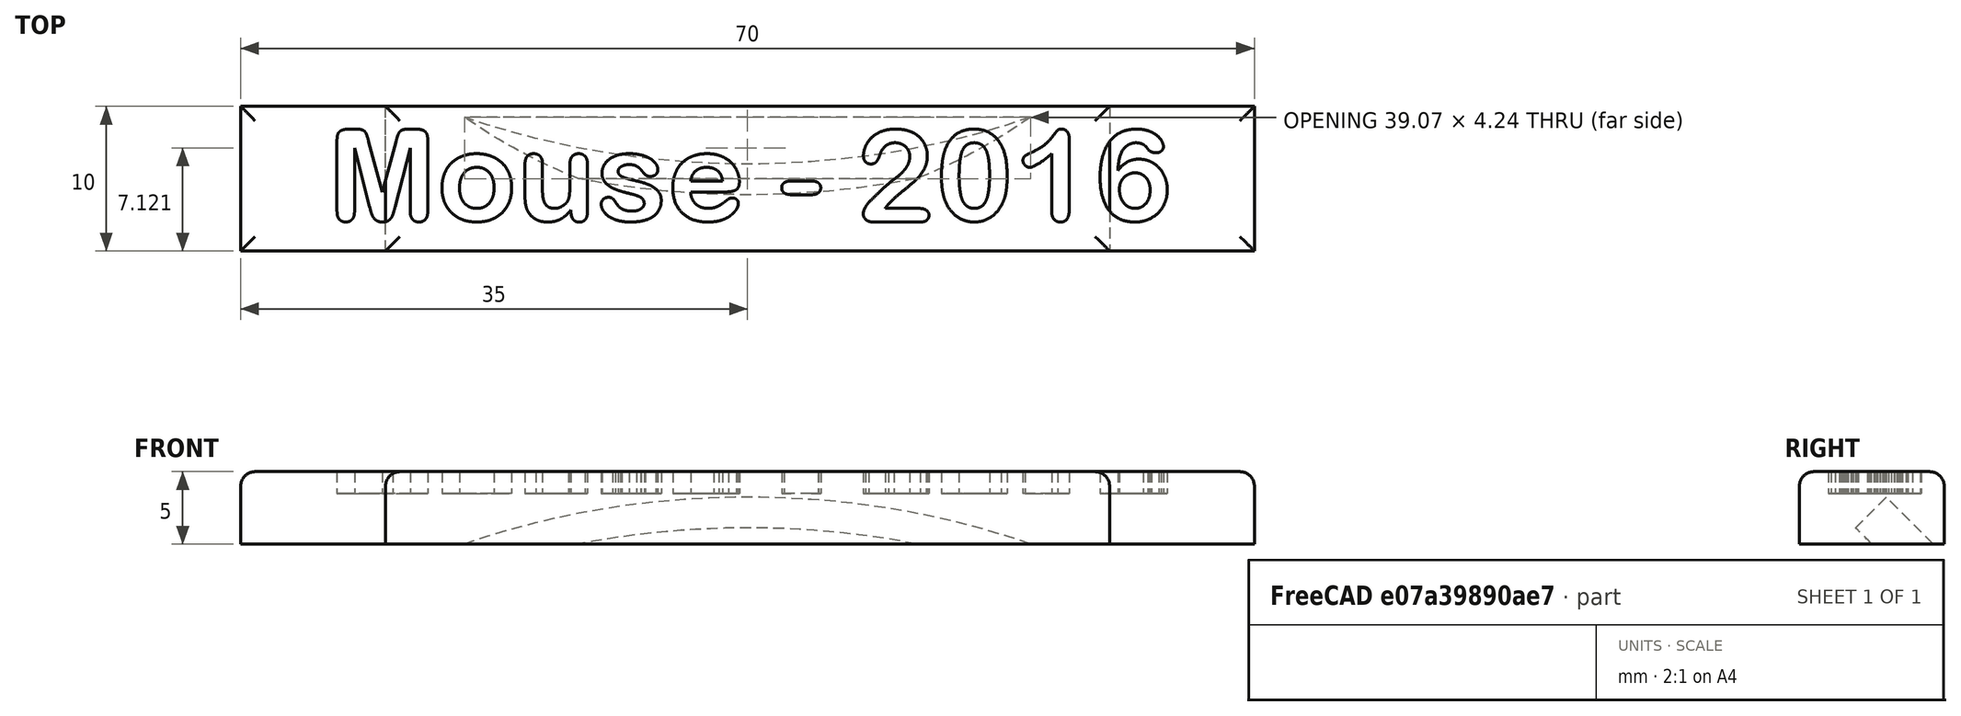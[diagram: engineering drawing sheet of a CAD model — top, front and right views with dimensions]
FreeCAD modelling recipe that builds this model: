
FCSTD DOCUMENT  (FreeCAD 0.19R24291 (Git))
Label: Name-Plate
License: All rights reserved
LicenseURL: http://en.wikipedia.org/wiki/All_rights_reserved
objects: Part::Part2DObjectPython×7, Sketcher::SketchObject×4, PartDesign::Pocket×3, PartDesign::Pad×2, PartDesign::Fillet×2, PartDesign::Body×2, PartDesign::Plane×1, Mesh::Feature×1
note: 28 computed .brp shape members not serialized (recipe doc carries the construction recipe); baked Part::Feature solids carry a one-line shape summary decoded from their .brp

FEATURE [Sketcher::SketchObject] Sketch
  FullyConstrained = true
  MapMode = 5
  Support = -> [XY_Plane]
  sketch-geometry (4):
    g0: LineSegment StartX=-25 StartY=0 StartZ=0 EndX=25 EndY=0 EndZ=0
    g1: LineSegment StartX=25 StartY=0 StartZ=0 EndX=25 EndY=-10 EndZ=0
    g2: LineSegment StartX=25 StartY=-10 StartZ=0 EndX=-25 EndY=-10 EndZ=0
    g3: LineSegment StartX=-25 StartY=-10 StartZ=0 EndX=-25 EndY=0 EndZ=0
  constraints (11):
    c: Coincident(g0,g1)
    c: Coincident(g1,g2)
    c: Coincident(g2,g3)
    c: Coincident(g3,g0)
    c: Horizontal(g0)
    c: Vertical(g1)
    c: Vertical(g3)
    c: PointOnObject(g0,g-1)
    c: Symmetric(g2,g1,g-2)
    c: DistanceY(g3,g3) = 10
    c: DistanceX(g2,g2) = 50
FEATURE [PartDesign::Pad] Pad
  Direction = (1,1,1)
  Length = 5
  Length2 = 100
  Profile = -> Sketch
  Type = 0
FEATURE [Part::Part2DObjectPython] ShapeString001  label="Trouble"  # Draft 2D object (typed FeaturePython)
  FontFile = /System/Library/Fonts/Supplemental/Arial Rounded Bold.ttf
  Size = 7
  String = Trouble - 2016
  Tracking = 0
FEATURE [Part::Part2DObjectPython] ShapeString002  label="Pretzel"  # Draft 2D object (typed FeaturePython)
  FontFile = /System/Library/Fonts/Supplemental/Arial Narrow Bold Italic.ttf
  Size = 7
  String = Pretzel - 2017
  Tracking = 0
FEATURE [Part::Part2DObjectPython] ShapeString003  label="Cajun"  # Draft 2D object (typed FeaturePython)
  FontFile = /System/Library/Fonts/Supplemental/Arial Narrow Bold Italic.ttf
  Size = 7
  String = Cajun - 2018
  Tracking = 0
FEATURE [Part::Part2DObjectPython] ShapeString004  label="Baguette"  # Draft 2D object (typed FeaturePython)
  FontFile = /System/Library/Fonts/Supplemental/Arial Narrow Bold Italic.ttf
  Size = 7
  String = Baguette - 2018
  Tracking = 0
FEATURE [Part::Part2DObjectPython] ShapeString005  label="Spice"  # Draft 2D object (typed FeaturePython)
  FontFile = /System/Library/Fonts/Supplemental/Arial Narrow Bold Italic.ttf
  Size = 7
  String = Spice - 2018
  Tracking = 0
FEATURE [Part::Part2DObjectPython] ShapeString006  label="Bunny"  # Draft 2D object (typed FeaturePython)
  FontFile = /System/Library/Fonts/Supplemental/Arial Narrow Bold Italic.ttf
  Size = 7
  String = Bunny - 2019
  Tracking = 0
FEATURE [Sketcher::SketchObject] Sketch001
  AttachmentOffset = pos=(0,-30,-25) rot=(1,0,0;0.785398rad)
  FullyConstrained = true
  MapMode = 5
  Placement = pos=(0,25,-30) rot=(1,0,0;2.35619rad)
  Support = -> [XZ_Plane]
  sketch-geometry (1):
    g0: Circle CenterX=0 CenterY=0 CenterZ=0 NormalX=0 NormalY=0 NormalZ=1 AngleXU=0 Radius=44
  constraints (2):
    c: Coincident(g0,g-1)
    c: Radius(g0) = 44
FEATURE [PartDesign::Pocket] Pocket
  BaseFeature = -> Pad
  Length = 3
  Length2 = 100
  Profile = -> Sketch001
  Type = 0
FEATURE [PartDesign::Fillet] Fillet
  Base = -> Pocket [Edge7,Edge16,Edge10,Edge4]
  BaseFeature = -> Pocket
  Radius = 1
  SupportTransform = false
FEATURE [PartDesign::Body] Body  label="Base Nameplace"
  Group = -> [Sketch,Pad,Sketch001,Pocket,Fillet]
  Origin = -> Origin
  Tip = -> Fillet
FEATURE [Sketcher::SketchObject] Sketch002
  AttachmentOffset = pos=(0,-27,-25) rot=(1,0,0;0.785398rad)
  FullyConstrained = true
  MapMode = 5
  Placement = pos=(0,25,-27) rot=(1,0,0;2.35619rad)
  Support = -> [XZ_Plane001]
  sketch-geometry (1):
    g0: Circle CenterX=0 CenterY=0 CenterZ=0 NormalX=0 NormalY=0 NormalZ=1 AngleXU=0 Radius=44
  constraints (2):
    c: Coincident(g0,g-1)
    c: Radius(g0) = 44
FEATURE [Sketcher::SketchObject] Sketch003
  FullyConstrained = true
  MapMode = 5
  Support = -> [XY_Plane001]
  sketch-geometry (4):
    g0: LineSegment StartX=-35 StartY=0 StartZ=0 EndX=35 EndY=0 EndZ=0
    g1: LineSegment StartX=35 StartY=0 StartZ=0 EndX=35 EndY=-10 EndZ=0
    g2: LineSegment StartX=35 StartY=-10 StartZ=0 EndX=-35 EndY=-10 EndZ=0
    g3: LineSegment StartX=-35 StartY=-10 StartZ=0 EndX=-35 EndY=0 EndZ=0
  constraints (11):
    c: Coincident(g0,g1)
    c: Coincident(g1,g2)
    c: Coincident(g2,g3)
    c: Coincident(g3,g0)
    c: Horizontal(g0)
    c: Vertical(g1)
    c: Vertical(g3)
    c: PointOnObject(g0,g-1)
    c: Symmetric(g2,g1,g-2)
    c: DistanceY(g3,g3) = 10
    c: DistanceX(g2,g2) = 70
FEATURE [PartDesign::Pad] Pad001
  Direction = (1,1,1)
  Length = 5
  Length2 = 100
  Profile = -> Sketch003
  Type = 0
FEATURE [PartDesign::Pocket] Pocket001
  BaseFeature = -> Pad001
  Length = 3
  Length2 = 100
  Profile = -> Sketch002
  Type = 0
FEATURE [PartDesign::Fillet] Fillet001
  Base = -> Pocket001 [Edge7,Edge16,Edge10,Edge4]
  BaseFeature = -> Pocket001
  Radius = 1
  SupportTransform = false
FEATURE [Part::Part2DObjectPython] ShapeString  label="Mouse"  # Draft 2D object (typed FeaturePython)
  AttachmentOffset = pos=(-29,-8,0) rot=(0,0,1;0rad)
  FontFile = /System/Library/Fonts/Supplemental/Arial Rounded Bold.ttf
  MapMode = 5
  Placement = pos=(-29,-8,5) rot=(0,0,1;0rad)
  Size = 7
  String = Mouse - 2016
  Support = -> [Fillet001]
  Tracking = 0
FEATURE [PartDesign::Pocket] Pocket002
  BaseFeature = -> Fillet001
  Length = 1.5
  Length2 = 100
  Profile = -> ShapeString
  Type = 0
FEATURE [PartDesign::Plane] DatumPlane
  Length = 104.897
  MapMode = 5
  Placement = pos=(0,0,5) rot=(0,0,1;0rad)
  ResizeMode = 0
  Support = -> [Fillet001]
  Width = 98.0099
FEATURE [PartDesign::Body] Body001  label="Mouse Nameplate"
  Group = -> [Sketch003,Pad001,Sketch002,Pocket001,Fillet001,DatumPlane,ShapeString,Pocket002]
  Origin = -> Origin001
  Tip = -> Pocket002
FEATURE [Mesh::Feature] Ferret
  Placement = pos=(-137,-142,0) rot=(0,0,1;0rad)
